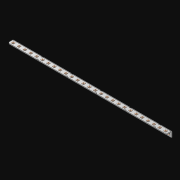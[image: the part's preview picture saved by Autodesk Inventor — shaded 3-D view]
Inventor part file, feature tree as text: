
AUTODESK INVENTOR PART (.ipt)
format: ipt  version: 2021 (Build 250183000, 183)  size: 795,136 bytes
history: native  units: in
note: dims shown in document units (in); Inventor stores cm internally (conversion verified against a paired STEP export)
features: extrude x55, other x54, sketch x3, pattern_linear x1, sheet_metal_op x1
ambient origin geometry x8: Origin, YZ Plane, XZ Plane, XY Plane, X Axis, Y Axis, Z Axis, Center Point
bodies: Solid1 (feature_tree)
feature tree (114):
  pattern_linear  "Rectangular Pattern1"  Spacing1=0.063in  [1 undecoded]
  extrude  "Extrusion1"  Depth=0.5in
  sketch  "Sketch1"  dims[d0=0.182in]
  other  "Srf1"
  sketch  "Sketch2"  dims[d1=0.063in d2=0.0in]
  other  "Srf2"
  other  "Srf3"
  other  "Srf5"
  other  "Srf7"
  other  "Srf9"
  other  "Srf11"
  other  "Srf13"
  other  "Srf15"
  other  "Srf17"
  other  "Srf19"
  other  "Srf21"
  other  "Srf23"
  other  "Srf25"
  other  "Srf27"
  other  "Srf29"
  other  "Srf31"
  other  "Srf33"
  other  "Srf35"
  other  "Srf37"
  other  "Srf39"
  other  "Srf41"
  other  "Srf43"
  other  "Srf45"
  other  "Srf47"
  other  "Srf49"
  other  "Srf51"
  other  "Srf53"
  other  "Srf4"
  other  "Srf6"
  other  "Srf8"
  other  "Srf10"
  other  "Srf12"
  other  "Srf14"
  other  "Srf16"
  other  "Srf18"
  other  "Srf20"
  other  "Srf22"
  other  "Srf24"
  other  "Srf26"
  other  "Srf28"
  other  "Srf30"
  other  "Srf32"
  other  "Srf34"
  other  "Srf36"
  other  "Srf38"
  other  "Srf40"
  other  "Srf42"
  other  "Srf44"
  other  "Srf46"
  other  "Srf48"
  other  "Srf50"
  other  "Srf52"
  other  "Srf54"
  sketch  "Sketch3"  dims[d3=0.182in d4=0.063in d5=0.0in d8=0.5in d9=4.0in d10=0.0in]
  sheet_metal_op  "Fold1"
  extrude  "ExtrusionSrf1"  Depth=0.5in TaperAngle=0.0deg
  extrude  "ExtrusionSrf2"  [1 undecoded]
  extrude  "ExtrusionSrf3"  [1 undecoded]
  extrude  "ExtrusionSrf4"  [1 undecoded]
  extrude  "ExtrusionSrf5"  [1 undecoded]
  extrude  "ExtrusionSrf6"  [1 undecoded]
  extrude  "ExtrusionSrf7"  [1 undecoded]
  extrude  "ExtrusionSrf8"  [1 undecoded]
  extrude  "ExtrusionSrf9"  [1 undecoded]
  extrude  "ExtrusionSrf10"  [1 undecoded]
  extrude  "ExtrusionSrf11"  [1 undecoded]
  extrude  "ExtrusionSrf12"  [1 undecoded]
  extrude  "ExtrusionSrf13"  [1 undecoded]
  extrude  "ExtrusionSrf14"  [1 undecoded]
  extrude  "ExtrusionSrf15"  [1 undecoded]
  extrude  "ExtrusionSrf16"  [1 undecoded]
  extrude  "ExtrusionSrf17"  [1 undecoded]
  extrude  "ExtrusionSrf18"  [1 undecoded]
  extrude  "ExtrusionSrf19"  [1 undecoded]
  extrude  "ExtrusionSrf20"  [1 undecoded]
  extrude  "ExtrusionSrf21"  [1 undecoded]
  extrude  "ExtrusionSrf22"  [1 undecoded]
  extrude  "ExtrusionSrf23"  [1 undecoded]
  extrude  "ExtrusionSrf24"  [1 undecoded]
  extrude  "ExtrusionSrf25"  [1 undecoded]
  extrude  "ExtrusionSrf26"  [1 undecoded]
  extrude  "ExtrusionSrf27"  [1 undecoded]
  extrude  "ExtrusionSrf28"  [1 undecoded]
  extrude  "ExtrusionSrf37"  [1 undecoded]
  extrude  "ExtrusionSrf38"  [1 undecoded]
  extrude  "ExtrusionSrf39"  [1 undecoded]
  extrude  "ExtrusionSrf40"  [1 undecoded]
  extrude  "ExtrusionSrf41"  [1 undecoded]
  extrude  "ExtrusionSrf42"  [1 undecoded]
  extrude  "ExtrusionSrf43"  [1 undecoded]
  extrude  "ExtrusionSrf44"  [1 undecoded]
  extrude  "ExtrusionSrf45"  [1 undecoded]
  extrude  "ExtrusionSrf46"  [1 undecoded]
  extrude  "ExtrusionSrf47"  [1 undecoded]
  extrude  "ExtrusionSrf48"  [1 undecoded]
  extrude  "ExtrusionSrf49"  [1 undecoded]
  extrude  "ExtrusionSrf50"  [1 undecoded]
  extrude  "ExtrusionSrf51"  [1 undecoded]
  extrude  "ExtrusionSrf52"  [1 undecoded]
  extrude  "ExtrusionSrf53"  [1 undecoded]
  extrude  "ExtrusionSrf54"  [1 undecoded]
  extrude  "ExtrusionSrf55"  [1 undecoded]
  extrude  "ExtrusionSrf56"  [1 undecoded]
  extrude  "ExtrusionSrf57"  [1 undecoded]
  extrude  "ExtrusionSrf58"  [1 undecoded]
  extrude  "ExtrusionSrf59"  [1 undecoded]
  extrude  "ExtrusionSrf60"  [1 undecoded]
  extrude  "ExtrusionSrf61"  [1 undecoded]
  extrude  "ExtrusionSrf62"  [1 undecoded]
note: 54 required parameter values undecoded (feature->parameter linkage not recoverable at this tier; creation-order binding heuristic only, values carry confidence <= 0.55)
